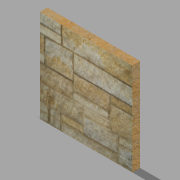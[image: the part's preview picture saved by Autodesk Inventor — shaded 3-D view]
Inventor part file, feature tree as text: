
AUTODESK INVENTOR PART (.ipt)
format: ipt  version: 2022.2 (Build 262287000, 287)  size: 133,120 bytes
history: native  units: in
note: dims shown in document units (in); Inventor stores cm internally (conversion verified against a paired STEP export)
features: extrude x1, sketch x1
ambient origin geometry x8: Origin, YZ Plane, XZ Plane, XY Plane, X Axis, Y Axis, Z Axis, Center Point
bodies: Body1 (feature_tree)
feature tree (2):
  extrude  "Extrusion2"  Depth=12.0in
  sketch  "Sketch2"  dims[d4=12.0in d5=12.0in d6=1.0in d7=0.0in]
